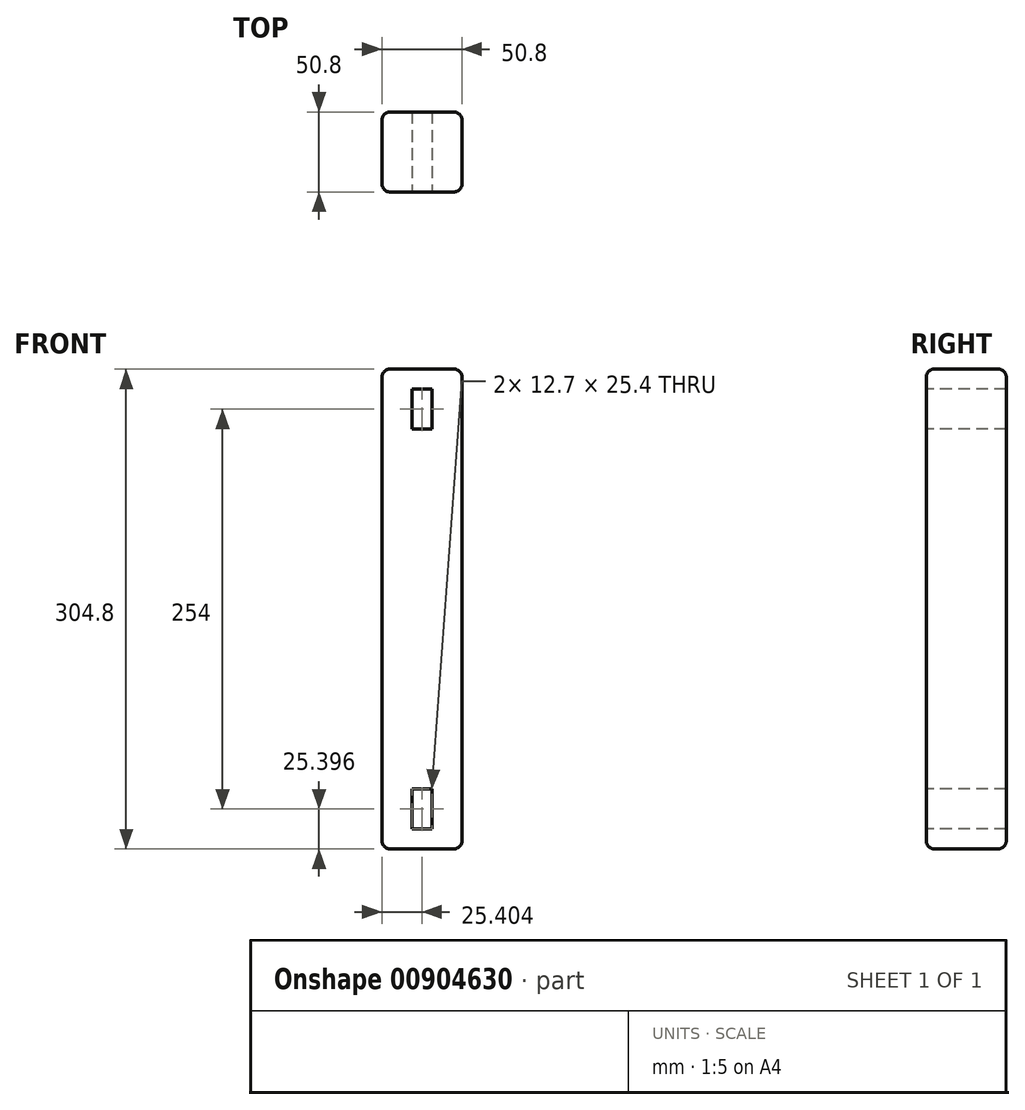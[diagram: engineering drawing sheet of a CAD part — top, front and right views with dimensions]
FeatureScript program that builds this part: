
annotation { "Feature Type Name" : "Feature", "Feature Type Description" : "" }
export const myFeature = defineFeature(function(context is Context, id is Id, definition is map)
    precondition{}
    {
        {
            var Q0;
            Q0=qCreatedBy(makeId("Front.planeOp"),FACE);
            var sketch = newSketch(context, id + "F0", { "sketchPlane" : qUnion([Q0])});
            skLineSegment(sketch, "E0.bottom", {"start": v(-25.68, 205.68) * mm, "end": v(25.12, 205.68) * mm});
            skLineSegment(sketch, "E0.top", {"start": v(-25.68, -99.12) * mm, "end": v(25.12, -99.12) * mm});
            skLineSegment(sketch, "E0.left", {"start": v(-25.68, 205.68) * mm, "end": v(-25.68, -99.12) * mm});
            skLineSegment(sketch, "E0.right", {"start": v(25.12, 205.68) * mm, "end": v(25.12, -99.12) * mm});
            skSolve(sketch);
        }
        {
            var Q0;
            Q0 = qSketchRegion(id + "F0", true);
            extrude(context, id + "F1", {"entities" : qUnion([Q0]), "endBound" : BoundingType.SYMMETRIC, "depth" : 50.8 * mm, "offsetDistance" : 25.4 * mm});
        }
        {
            var Q0;
            Q0=makeQuery(id+"F1.opExtrude","CAP_EDGE",EDGE,{"disambiguationData":[OSD([sQuery(id+"F0.wireOp",EDGE,"E0.right")])],"isStart":false});
            var Q1;
            Q1=makeQuery(id+"F1.opExtrude","CAP_EDGE",EDGE,{"disambiguationData":[OSD([sQuery(id+"F0.wireOp",EDGE,"E0.right")])],"isStart":true});
            var Q2;
            Q2=makeQuery(id+"F1.opExtrude","CAP_EDGE",EDGE,{"disambiguationData":[OSD([sQuery(id+"F0.wireOp",EDGE,"E0.left")])],"isStart":true});
            var Q3;
            Q3=makeQuery(id+"F1.opExtrude","CAP_EDGE",EDGE,{"disambiguationData":[OSD([sQuery(id+"F0.wireOp",EDGE,"E0.left")])],"isStart":false});
            var Q4;
            Q4=makeQuery(id+"F1.opExtrude","SWEPT_FACE",FACE,{"disambiguationData":[OSD([sQuery(id+"F0.wireOp",EDGE,"E0.bottom")])]});
            var Q5;
            Q5=makeQuery(id+"F1.opExtrude","SWEPT_FACE",FACE,{"disambiguationData":[OSD([sQuery(id+"F0.wireOp",EDGE,"E0.top")])]});
            fillet(context, id + "F2", {"entities" : qUnion([Q0, Q1, Q2, Q3, Q4, Q5]), "radius" : 5.08 * mm, "tangentPropagation" : true, "allowEdgeOverflow" : false});
        }
        {
            var Q0;
            Q0=makeQuery(id+"F1.opExtrude","CAP_FACE",FACE,{"disambiguationData":[OSD([sQuery(id+"F0.wireOp",EDGE,"E0.bottom"),sQuery(id+"F0.wireOp",EDGE,"E0.top"),sQuery(id+"F0.wireOp",EDGE,"E0.left"),sQuery(id+"F0.wireOp",EDGE,"E0.right")])],"isStart":false});
            var sketch = newSketch(context, id + "F3", { "sketchPlane" : qUnion([Q0])});
            skLineSegment(sketch, "E1.bottom", {"start": v(-6.63, 192.98) * mm, "end": v(6.07, 192.98) * mm});
            skLineSegment(sketch, "E1.top", {"start": v(-6.63, 167.58) * mm, "end": v(6.07, 167.58) * mm});
            skLineSegment(sketch, "E1.left", {"start": v(-6.63, 192.98) * mm, "end": v(-6.63, 167.58) * mm});
            skLineSegment(sketch, "E1.right", {"start": v(6.07, 192.98) * mm, "end": v(6.07, 167.58) * mm});
            skSolve(sketch);
        }
        {
            var Q0;
            Q0 = qSketchRegion(id + "F3", true);
            extrude(context, id + "F4", {"entities" : qUnion([Q0]), "operationType" : NewBodyOperationType.REMOVE, "endBound" : BoundingType.THROUGH_ALL, "oppositeDirection" : true, "depth" : 25.4 * mm, "offsetDistance" : 25.4 * mm});
        }
        {
            var Q0;
            Q0=makeQuery(id+"F1.opExtrude","CAP_FACE",FACE,{"disambiguationData":[OSD([sQuery(id+"F0.wireOp",EDGE,"E0.bottom"),sQuery(id+"F0.wireOp",EDGE,"E0.top"),sQuery(id+"F0.wireOp",EDGE,"E0.left"),sQuery(id+"F0.wireOp",EDGE,"E0.right")])],"isStart":false});
            var sketch = newSketch(context, id + "F5", { "sketchPlane" : qUnion([Q0])});
            skLineSegment(sketch, "E2.bottom", {"start": v(-6.63, -61.02) * mm, "end": v(6.07, -61.02) * mm});
            skLineSegment(sketch, "E2.top", {"start": v(-6.63, -86.42) * mm, "end": v(6.07, -86.42) * mm});
            skLineSegment(sketch, "E2.left", {"start": v(-6.63, -61.02) * mm, "end": v(-6.63, -86.42) * mm});
            skLineSegment(sketch, "E2.right", {"start": v(6.07, -61.02) * mm, "end": v(6.07, -86.42) * mm});
            skSolve(sketch);
        }
        {
            var Q0;
            Q0 = qSketchRegion(id + "F5", true);
            extrude(context, id + "F6", {"entities" : qUnion([Q0]), "operationType" : NewBodyOperationType.REMOVE, "endBound" : BoundingType.THROUGH_ALL, "oppositeDirection" : true, "depth" : 25.4 * mm, "offsetDistance" : 25.4 * mm});
        }
    });
